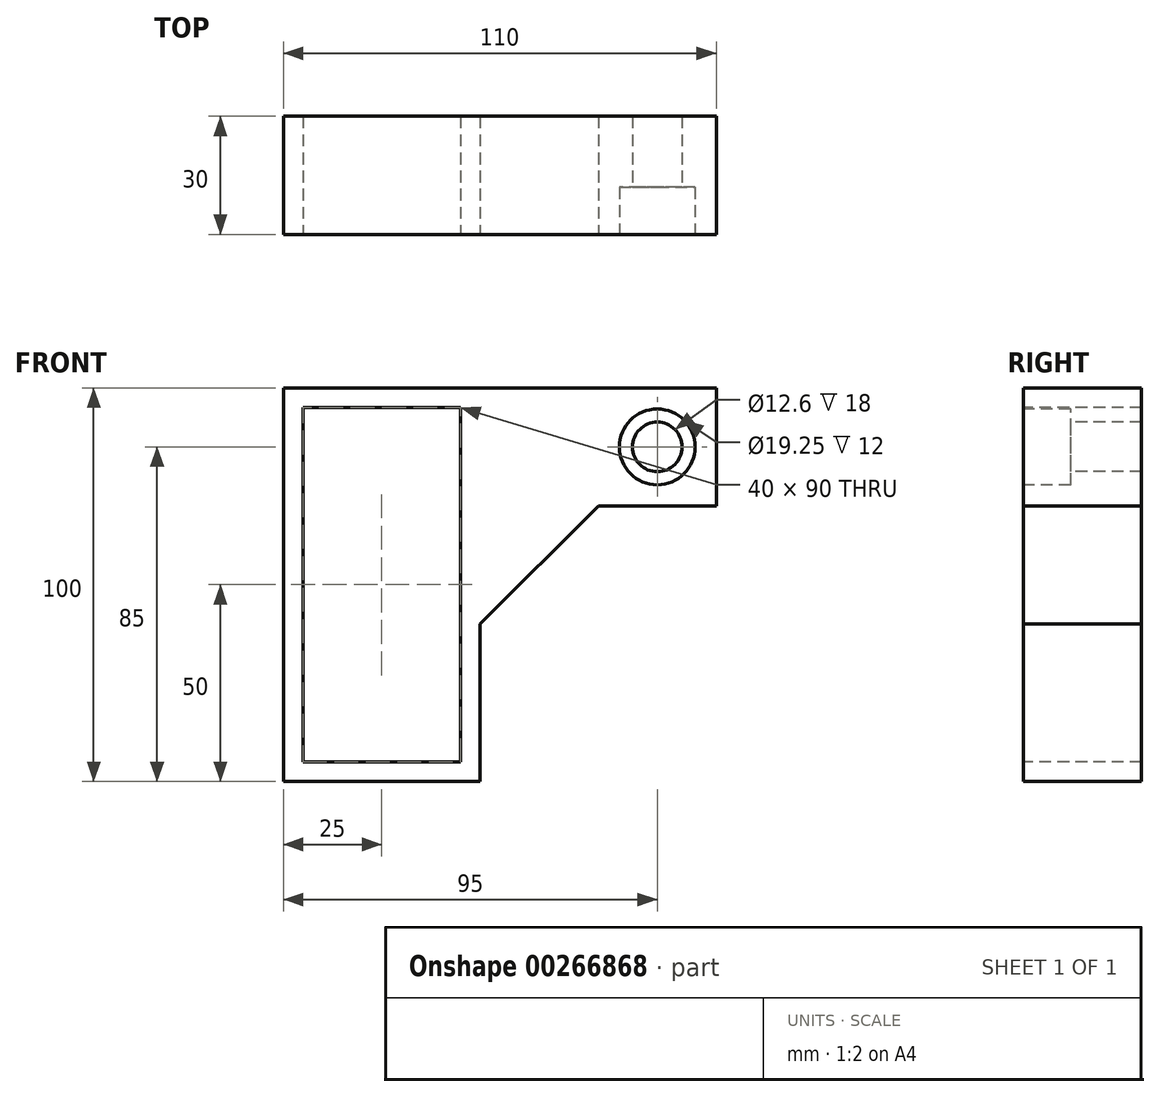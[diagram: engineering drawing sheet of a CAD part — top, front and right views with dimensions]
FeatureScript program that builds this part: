
annotation { "Feature Type Name" : "Feature", "Feature Type Description" : "" }
export const myFeature = defineFeature(function(context is Context, id is Id, definition is map)
    precondition{}
    {
        {
            var Q0;
            Q0=qCreatedBy(makeId("Front.planeOp"),FACE);
            var sketch = newSketch(context, id + "F0", { "sketchPlane" : qUnion([Q0])});
            skLineSegment(sketch, "E0", {"start": v(0, 0) * mm, "end": v(0, -40) * mm});
            skLineSegment(sketch, "E1", {"start": v(0, 0) * mm, "end": v(0, 30) * mm, "construction": true});
            skLineSegment(sketch, "E2", {"start": v(0, 0) * mm, "end": v(30, 30) * mm});
            skLineSegment(sketch, "E3", {"start": v(0, 0) * mm, "end": v(60, 0) * mm, "construction": true});
            skLineSegment(sketch, "E4", {"start": v(0, -40) * mm, "end": v(-50, -40) * mm});
            skLineSegment(sketch, "E5", {"start": v(-50, -40) * mm, "end": v(-50, 60) * mm});
            skLineSegment(sketch, "E6", {"start": v(30, 30) * mm, "end": v(60, 30) * mm});
            skLineSegment(sketch, "E7", {"start": v(-50, 60) * mm, "end": v(60, 60) * mm});
            skLineSegment(sketch, "E8", {"start": v(60, 60) * mm, "end": v(60, 30) * mm});
            skLineSegment(sketch, "E9", {"start": v(60, 45) * mm, "end": v(45, 45) * mm, "construction": true});
            skPoint(sketch, "E10", {"position": v(45, 45) * mm});
            skLineSegment(sketch, "E11", {"start": v(-50, -40) * mm, "end": v(-50, -35) * mm, "construction": true});
            skLineSegment(sketch, "E12", {"start": v(-50, -35) * mm, "end": v(-45, -35) * mm, "construction": true});
            skLineSegment(sketch, "E13", {"start": v(-45, -35) * mm, "end": v(-45, 55) * mm});
            skLineSegment(sketch, "E14", {"start": v(-45, 55) * mm, "end": v(-5, 55) * mm});
            skLineSegment(sketch, "E15", {"start": v(-5, 55) * mm, "end": v(-5, -35) * mm});
            skLineSegment(sketch, "E16", {"start": v(-5, -35) * mm, "end": v(-45, -35) * mm});
            skLineSegment(sketch, "E17", {"start": v(-25, 55) * mm, "end": v(-25, -35) * mm, "construction": true});
            skLineSegment(sketch, "E18", {"start": v(-25, 10) * mm, "end": v(-35, 10) * mm, "construction": true});
            skLineSegment(sketch, "E19", {"start": v(-35, 10) * mm, "end": v(-35, 40) * mm});
            skLineSegment(sketch, "E20.MirrorCS", {"start": v(-15, 10) * mm, "end": v(-15, 40) * mm});
            skLineSegment(sketch, "E21.MirrorCS", {"start": v(-35, 10) * mm, "end": v(-35, -20) * mm});
            skLineSegment(sketch, "E22.MirrorCS", {"start": v(-15, 10) * mm, "end": v(-15, -20) * mm});
            skPoint(sketch, "E23", {"position": v(-25, 30) * mm});
            skPoint(sketch, "E24.MirrorP", {"position": v(-25, -10) * mm});
            skLineSegment(sketch, "E25", {"start": v(-30, 30) * mm, "end": v(-30, 10) * mm});
            skLineSegment(sketch, "E26.MirrorCS", {"start": v(-30, -10) * mm, "end": v(-30, 10) * mm});
            skLineSegment(sketch, "E27.MirrorCS", {"start": v(-20, 30) * mm, "end": v(-20, 10) * mm});
            skLineSegment(sketch, "E28.MirrorCS", {"start": v(-20, -10) * mm, "end": v(-20, 10) * mm});
            skArc(sketch, "E29", {"start": v(-20, 30) * mm, "mid": v(-25, 35) * mm, "end": v(-30, 30) * mm});
            skArc(sketch, "E30", {"start": v(-30, -10) * mm, "mid": v(-25, -15) * mm, "end": v(-20, -10) * mm});
            skCircle(sketch, "E31", {"center": v(-25, 30) * mm, "radius": 10 * mm});
            skSolve(sketch);
        }
        {
            var Q0;
            Q0=makeQuery(id+"F0.imprint","IMPRINT",FACE,{"disambiguationData":[TD([[makeQuery(id+"F0.imprint","IMPRINT",EDGE,{"derivedFrom":sQuery(id+"F0.wireOp",EDGE,"E0")}),-1.0]])]});
            extrude(context, id + "F1", {"entities" : qUnion([Q0]), "oppositeDirection" : true, "depth" : 30 * mm});
        }
        {
            var Q0;
            Q0=sQuery(id+"F0.wireOp",VERTEX,"E10");
            var Q1;
            Q1=makeQuery(id+"F1.opExtrude","SWEPT_BODY",BODY,{"disambiguationData":[OSD([sQuery(id+"F0.wireOp",EDGE,"E0"),sQuery(id+"F0.wireOp",EDGE,"E2"),sQuery(id+"F0.wireOp",EDGE,"E4"),sQuery(id+"F0.wireOp",EDGE,"E5"),sQuery(id+"F0.wireOp",EDGE,"E6"),sQuery(id+"F0.wireOp",EDGE,"E7"),sQuery(id+"F0.wireOp",EDGE,"E8")])]});
            hole(context, id + "F2", {"style" : HoleStyle.C_BORE, "endStyle" : HoleEndStyle.THROUGH, "standardTappedOrClearance" : lookupTablePath({ "standard" : "ISO", "fit" : "Close", "size" : "M12", "type" : "Clearance" }), "standardBlindInLast" : lookupTablePath({ "fit" : "Close", "standard" : "ISO", "size" : "M12", "type" : "Clearance" }), "holeDiameter" : 12.6 * mm, "cBoreDiameter" : 19.25 * mm, "cBoreDepth" : 12 * mm, "tappedDepth" : 12 * mm, "tapClearance" : 3, "locations" : qUnion([Q0]), "scope" : qUnion([Q1])});
        }
    });
